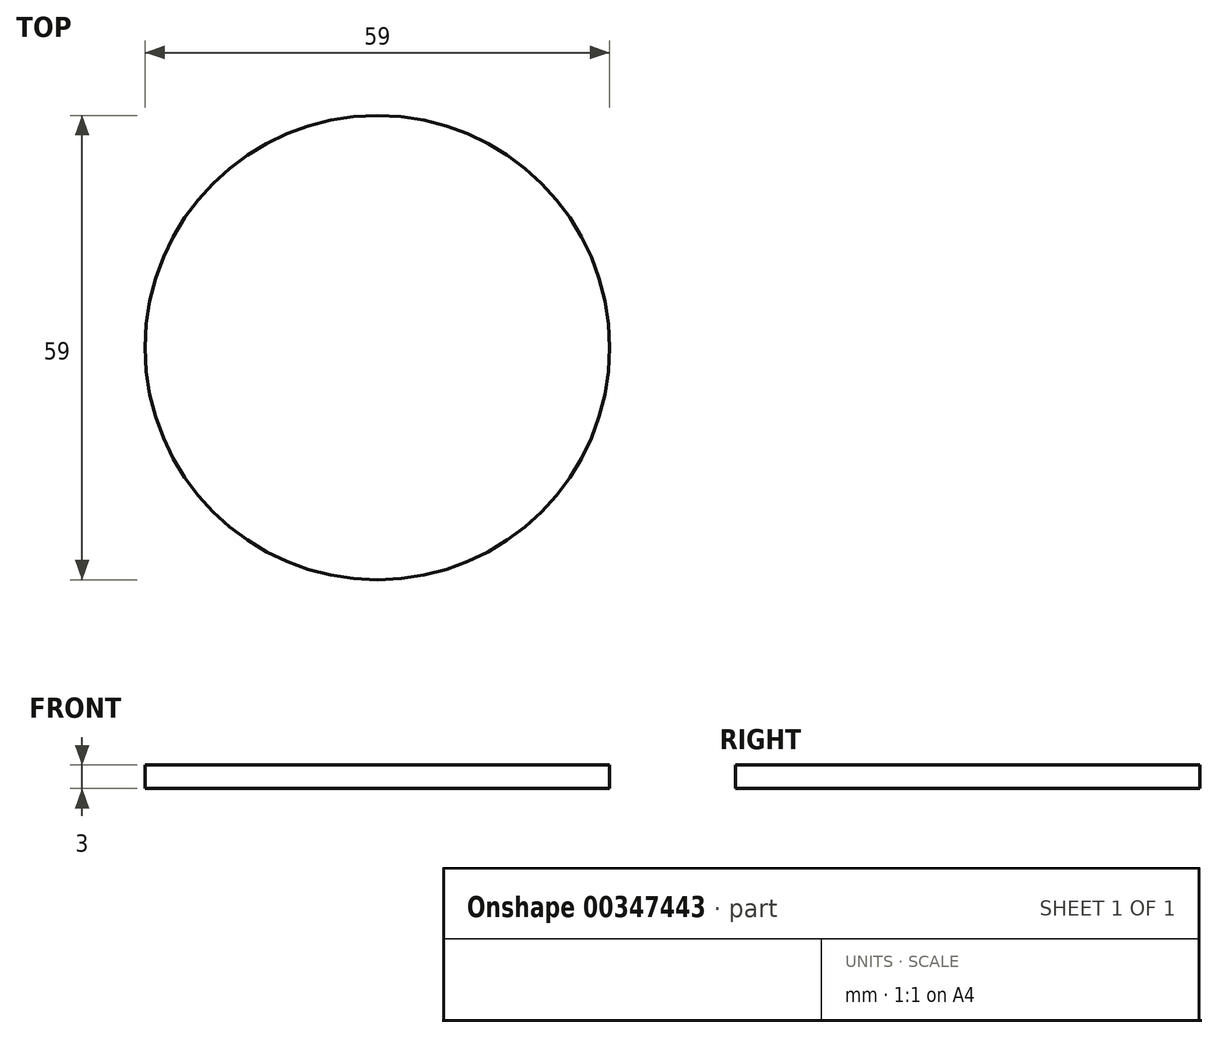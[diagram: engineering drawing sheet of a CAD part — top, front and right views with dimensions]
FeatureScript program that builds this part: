
annotation { "Feature Type Name" : "Feature", "Feature Type Description" : "" }
export const myFeature = defineFeature(function(context is Context, id is Id, definition is map)
    precondition{}
    {
        {
            var Q0;
            Q0=qCreatedBy(makeId("Top.planeOp"),FACE);
            var sketch = newSketch(context, id + "F0", { "sketchPlane" : qUnion([Q0])});
            skCircle(sketch, "E0", {"center": v(0, 0) * mm, "radius": 29.5 * mm});
            skSolve(sketch);
        }
        {
            var Q0;
            Q0=makeQuery(id+"F0.imprint","IMPRINT",FACE,{"disambiguationData":[TD([[makeQuery(id+"F0.imprint","IMPRINT",EDGE,{"derivedFrom":sQuery(id+"F0.wireOp",EDGE,"E0")}),1.0]])]});
            extrude(context, id + "F1", {"entities" : qUnion([Q0]), "depth" : 3 * mm});
        }
    });
